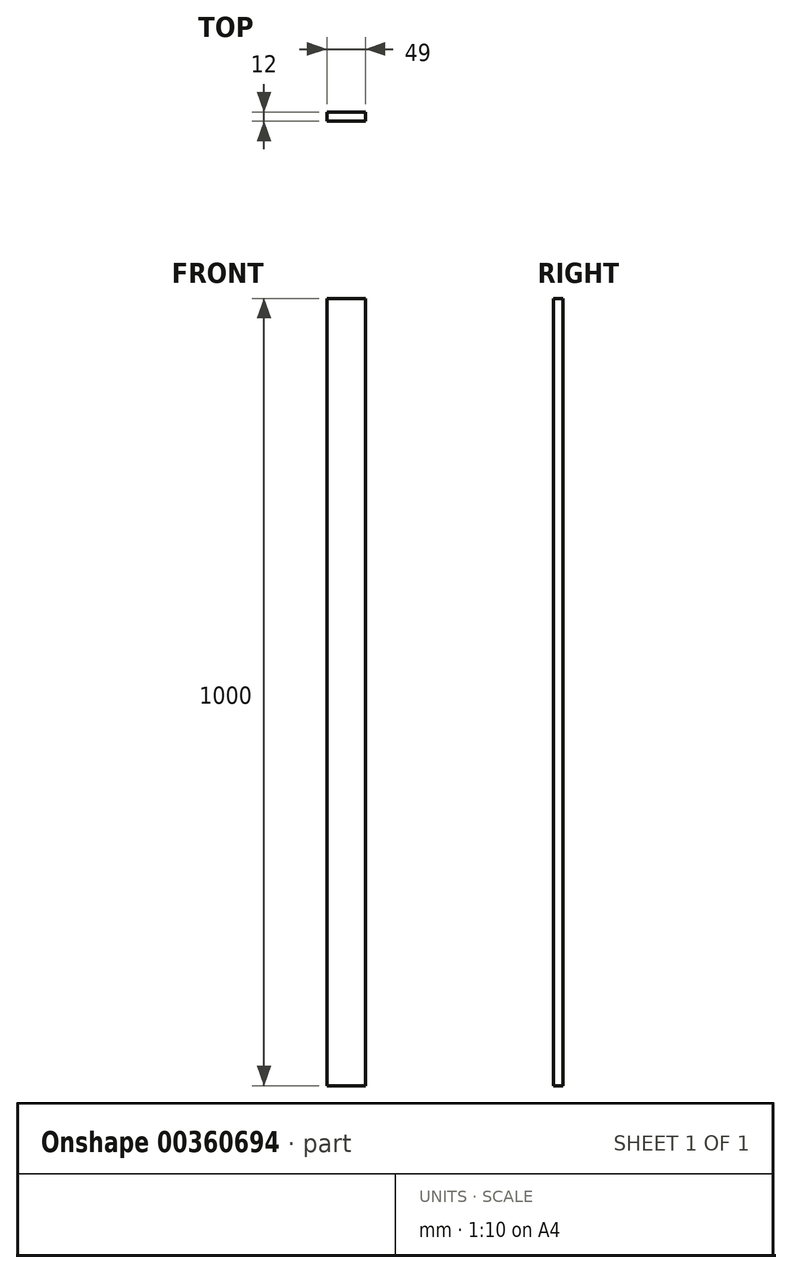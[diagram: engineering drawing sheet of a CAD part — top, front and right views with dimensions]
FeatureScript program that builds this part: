
annotation { "Feature Type Name" : "Feature", "Feature Type Description" : "" }
export const myFeature = defineFeature(function(context is Context, id is Id, definition is map)
    precondition{}
    {
        {
            var Q0;
            Q0=qCreatedBy(makeId("Front.planeOp"),FACE);
            var sketch = newSketch(context, id + "F0", { "sketchPlane" : qUnion([Q0])});
            skLineSegment(sketch, "E0.bottom", {"start": v(0, 0) * mm, "end": v(49, 0) * mm});
            skLineSegment(sketch, "E0.top", {"start": v(0, 1000) * mm, "end": v(49, 1000) * mm});
            skLineSegment(sketch, "E0.left", {"start": v(0, 0) * mm, "end": v(0, 1000) * mm});
            skLineSegment(sketch, "E0.right", {"start": v(49, 0) * mm, "end": v(49, 1000) * mm});
            skSolve(sketch);
        }
        {
            var Q0;
            Q0=makeQuery(id+"F0.imprint","IMPRINT",FACE,{"disambiguationData":[TD([[makeQuery(id+"F0.imprint","IMPRINT",EDGE,{"derivedFrom":sQuery(id+"F0.wireOp",EDGE,"E0.bottom")}),1.0]])]});
            extrude(context, id + "F1", {"entities" : qUnion([Q0]), "depth" : 12 * mm});
        }
    });
